# Revit family: Titus CBE2-24 Wide, Linear Chilled Beam, Face Hosted, Revit20,v0
name_source: partatom
category: Mechanical Equipment
units: mm (PartAtom-declared; Revit-internal decimal feet)

## family parameters
Cut with Voids When Loaded = Yes
Host = Face
OmniClass Number = 23.75.70.17.31
OmniClass Title = Induction Units
Part Type = Normal
Room Calculation Point = No
Round Connector Dimension = Use Radius
Shared = No

## types (1)
- CBAL2-24 LAY-IN
    1/2" In MNPT = No
    1/2" in Sweat = No
    10 Feet = No
    10" Oval = No
    2 - Two-way,Throw = No
    2 Feet = Yes
    2-Pipe System = No
    24" Wide Beam = Yes
    26 - White = Yes
    2P1C - 2 Pipe, 1 Coil Circuit = No
    2P2C - 2 Pipe, 2 Coil Circuit = No
    3 - LAY-IN = Yes
    3 Feet = No
    3/4" In MNPT = Yes
    4 Feet = No
    4" Dia. = Yes
    4-Pipe System = Yes
    4P1C - 4 Pipe, 1 Coil Circuit = Yes
    4P2C - 4 Pipe, 2 Coil Circuit = No
    5 Feet = No
    5" Dia. = No
    6 Feet = No
    6" Dia. = No
    7 Feet = No
    8 Feet = No
    8" Oval = No
    84 - Black = No
    9 Feet = No
    Actual Coefficient of Performance = 0
    Actual Cooling Entering Dry Bulb Temperature = 0 °F
    Actual Cooling Entering Wet Bulb Temperature = 0 °F
    Actual Cooling Leaving Dry Bulb Temperature = 0 °F
    Actual Cooling Leaving Wet Bulb Temperature = 0 °F
    Actual Energy Efficiency Rating (BTU/h.W) = 0
    Actual External Static Pressure = 0.00 in-wg
    Actual Filter Face Area = 0 SF
    Actual Full Load Efficiency = 0
    Actual Heating Entering Dry Bulb Temperature = 0 °F
    Actual Heating Leaving Dry Bulb Temperature = 0 °F
    Actual Height = 8 3/8"
    Actual Oval Width = 9 3/8"
    Actual Oval height = 5 1/4"
    Actual Radius = 1 15/16"
    Actual Total Static Pressure = 0.00 in-wg
    B - One-way, Back = No
    CTRL Angle = 90.00°
    CTRL Multi-Inlet Angle = 0.00°
    CTRL Multi-Inlet Connector Offset = 6 5/64"
    CTRL Multi-Inlet Offset = 5"
    CTRL Multi-Inlet Oval Angle = 0.00°
    CTRL Multi-Inlet Oval Connector Offset = 6 5/64"
    CTRL Multi-Inlet Round Angle = 0.00°
    CTRL Multi-Inlet Round Connector Offset = 6 5/64"
    CTRL Offset = 0"
    CTRL Oval Connector Offset = 4"
    CTRL Perforation Hole Dia = 1/8"
    CTRL Perforation Offset = 1/2"
    CTRL Pipe Connector Offset = 1 43/64"
    CTRL Round Connector Offset = 0"
    CTRL Thickness = 1/16"
    CWR Outlet Description = CWR-Outlet
    CWR Ver Offset = 10 3/4"
    CWS Inlet Description = CWS Inlet
    CWS Ver Offset = 11 7/8"
    Coil Material = Metal - Copper
    Condenser Inlet Radius = 1/4"
    Condenser Outlet Radius = 1/4"
    Condenser Pressure Drop = 0.00 psi
    Conditioned Air (Oval) Description = Disabled
    Conditioned Air (Round) Description = Conditioned Air
    Conditioned Air Connection Height = 1/2"
    Conditioned Air Connection Radius = 2"
    Conditioned Air Connection Width = 1/2"
    Connector Offset = 6 5/64"
    Default Elevation = 0"
    Description = Linear Chilled Beam Diffuser, Ceiling Mounted
    Design Ambient Summer Dry Bulb Temperature = 0 °F
    Design Ambient Winter Dry Bulb Temperature = 0 °F
    Design Ambient summer Wet bulb Temperature = 0 °F
    Design Cooling Minimum Air Flow = 0 CFM
    Design Heating Maximum Air Flow = 0 CFM
    Design Heating Minimum Air Flow = 0 CFM
    Design cooling Maximum Air Flow = 0 CFM
    Evaporator Inlet Radius = 1/4"
    Evaporator Outlet Radius = 1/4"
    Evaporator Pressure Drop = 0.00 psi
    F = 4 1/2"
    F - One-way, Front = Yes
    Frame Extension = 3/8"
    G = 4"
    H12 - SS Flex Hose - 12in = No
    H18 - SS Flex Hose - 18in = No
    H24 - SS Flex Hose - 24in = No
    HWR Description = HWR Outlet
    HWR Ver Offset = 13 1/4"
    HWS Inlet Description = HWS Inlet
    HWS Ver Offset = 14 3/8"
    Hanger Dimension F = 4 1/2"
    Hanger Visibility = No
    Hanger hole Length = 1 3/8"
    Height = 10 1/8"
    Hor Chilled Water Return Offset = 7 1/8"
    Hor Chilled Water Supply Offset = 7 3/4"
    Hor Hot Water Return Offset = 2 1/2"
    Hor Hot Water Supply Offset = 2 1/2"
    Inner Length = 21 5/8"
    Inner Width = 23 3/8"
    Input your Special Finish's name = Input your Special Finish's name
    Lay In Width = 23 3/4"
    Layin depath = 5/16"
    M13 = Yes
    M17 = No
    M20 = No
    M23 = No
    M27 = No
    M31 = No
    Manufacturer = Titus HVAC
    Material = Galvanized G90
    Model = CBE2-24
    Multi-Inlet = No
    NT - Tegular 9/16 Inch = No
    Pipe Connections Left Hand = Yes
    Pipe Connections Right Hand = No
    Pipe Height = 6"
    Primary Air Extension = 2 5/8"
    Primary Air Ver Offset = 6 1/8"
    Select Border Type = 1
    Select a Beam Length = 1
    Select a Piping Connection Type = 3
    Select a Water Coil Connection = 1
    Select a Water-Coil Type = 2
    Select an Air Inlet Dia = 1
    Select an Air Inlet Location = 2
    Select an Air Nozzle Configuration = 1
    Select an Air Throw Pattern = 2
    Select an Exposed Face Finish = 1
    Show Oval Connector = No
    Show Room Tag = No
    Show Round Connector = Yes
    Side Middle = No
    Side Plate = No
    Top Middle = Yes
    Top Plate = Yes
    Total Length = 22"
    Total Width = 31 3/8"

## geometry (parser evidence)
native form markers: Sweep x29
no freeform markers — native parametric forms only
